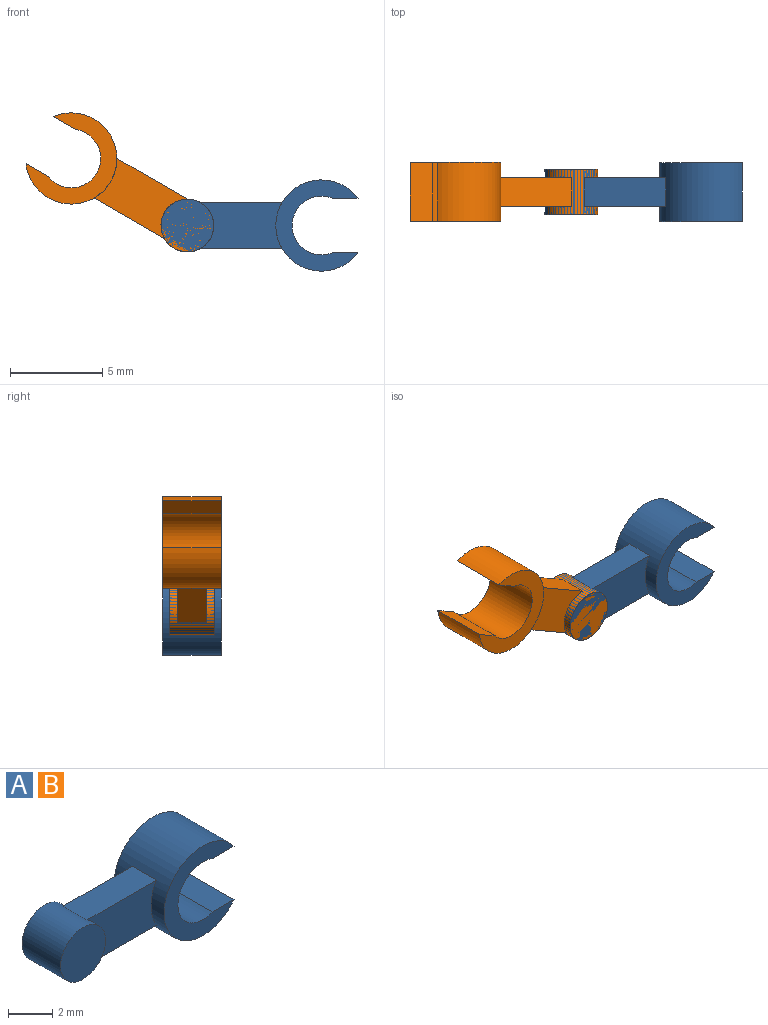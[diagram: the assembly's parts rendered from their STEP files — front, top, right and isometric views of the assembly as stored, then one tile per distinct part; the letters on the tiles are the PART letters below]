
ASSEMBLY  parts=2 mates=1
PART A: 13 faces, bbox 10.7x3.2x4.9 mm
  f0: cylinder r=2.47mm len=4.94mm, axis (0,1,0), area 35.4mm2, adj f3,f4,f5,f7,f8,f9,f10,f11
  f1: cylinder r=1.43mm len=2.86mm, axis (0,1,0), area 17.5mm2, adj f2,f3,f4,f5,f11,f12
  f2: plane 2.86x2.86mm, normal (0,-1,0), area 6.4mm2, adj f1
  f3: plane 4.41x1.53mm, normal (0,0,-1), area 6.7mm2, adj f0,f1,f5,f11
  f4: plane 4.41x1.53mm, normal (0,0,1), area 6.7mm2, adj f0,f1,f5,f11
  f5: plane 4.41x2.48mm, normal (0,-1,0), area 9.1mm2, adj f0,f1,f3,f4
  f6: cylinder r=1.59mm len=3.19mm, axis (0,1,0), area 19.8mm2, adj f7,f8,f9,f10
  f7: plane 3.19x1.39mm, normal (0,0,-1), area 4.4mm2, adj f0,f6,f9,f10
  f8: plane 3.19x1.39mm, normal (0,0,1), area 4.4mm2, adj f0,f6,f9,f10
  f9: plane 4.94x4.45mm, normal (0,-1,0), area 8.3mm2, adj f0,f6,f7,f8
  f10: plane 4.94x4.45mm, normal (0,1,0), area 8.3mm2, adj f0,f6,f7,f8
  f11: plane 4.41x2.48mm, normal (0,1,0), area 9.1mm2, adj f0,f1,f3,f4
  f12: plane 2.86x2.86mm, normal (0,1,0), area 6.4mm2, adj f1
PART B: same geometry as A
PLACE A t=(-4.62,0,-2.2)mm
PLACE B rot(axis=(0,-1,0),150deg) t=(-18.16,0,1.43)mm
MATE revolute B.f1 <-> A.f1  axis (0,1,0) through (-11.88,1.23,-2.2)mm
